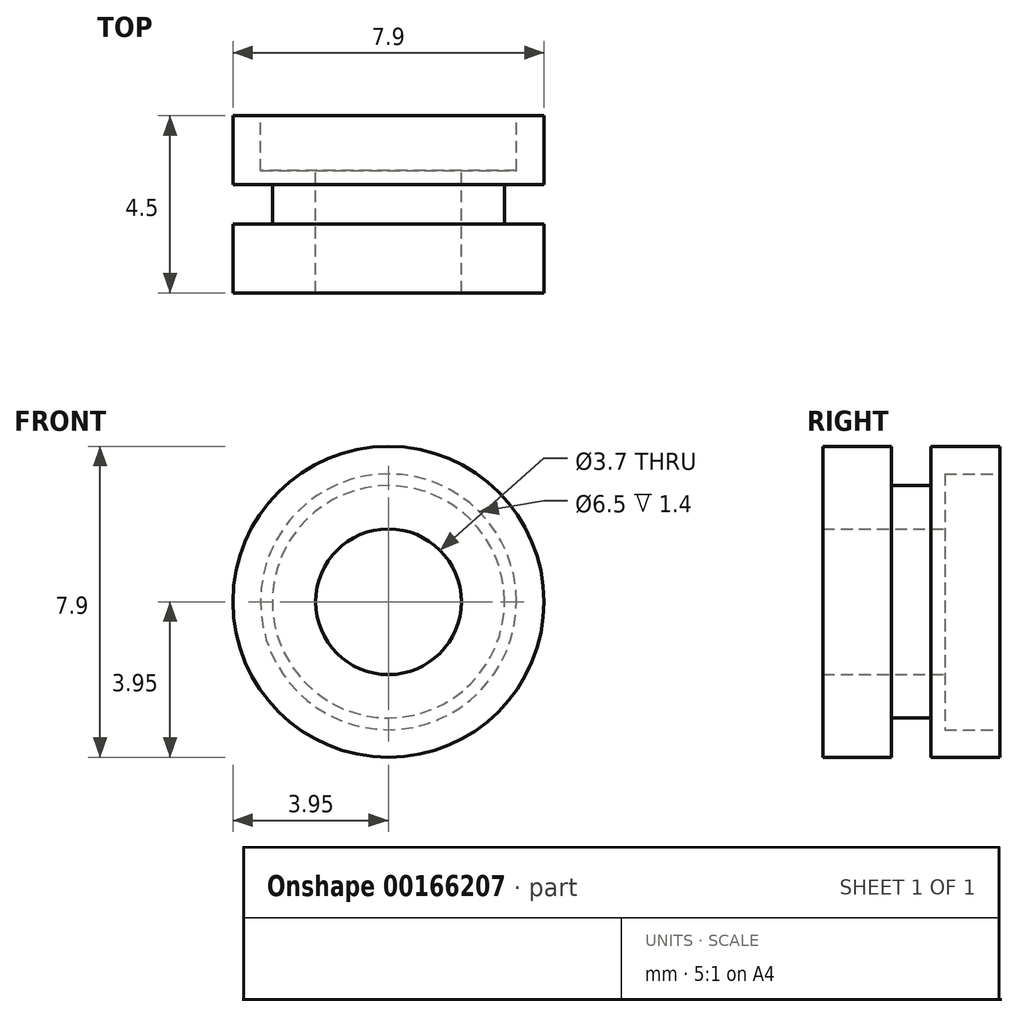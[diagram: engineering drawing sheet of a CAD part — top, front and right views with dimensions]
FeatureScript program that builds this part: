
annotation { "Feature Type Name" : "Feature", "Feature Type Description" : "" }
export const myFeature = defineFeature(function(context is Context, id is Id, definition is map)
    precondition{}
    {
        {
            var Q0;
            Q0=qCreatedBy(makeId("Right.planeOp"),FACE);
            var sketch = newSketch(context, id + "F0", { "sketchPlane" : qUnion([Q0])});
            skLineSegment(sketch, "E0", {"start": v(11.47, 0) * mm, "end": v(0, 0) * mm, "construction": true});
            skLineSegment(sketch, "E1", {"start": v(3.1, 1.85) * mm, "end": v(0, 1.85) * mm});
            skLineSegment(sketch, "E2", {"start": v(3.1, 1.85) * mm, "end": v(3.1, 3.25) * mm});
            skLineSegment(sketch, "E3", {"start": v(4.5, 3.25) * mm, "end": v(3.1, 3.25) * mm});
            skLineSegment(sketch, "E4", {"start": v(4.5, 3.25) * mm, "end": v(4.5, 3.95) * mm});
            skLineSegment(sketch, "E5", {"start": v(2.75, 3.95) * mm, "end": v(4.5, 3.95) * mm});
            skLineSegment(sketch, "E6", {"start": v(2.75, 3.95) * mm, "end": v(2.75, 2.95) * mm});
            skLineSegment(sketch, "E7", {"start": v(1.75, 2.95) * mm, "end": v(2.75, 2.95) * mm});
            skLineSegment(sketch, "E8", {"start": v(1.75, 2.95) * mm, "end": v(1.75, 3.95) * mm});
            skLineSegment(sketch, "E9", {"start": v(0, 3.95) * mm, "end": v(1.75, 3.95) * mm});
            skLineSegment(sketch, "E10", {"start": v(0, 3.95) * mm, "end": v(0, 1.85) * mm});
            skSolve(sketch);
        }
        {
            var Q0;
            Q0=makeQuery(id+"F0.imprint","IMPRINT",FACE,{"disambiguationData":[TD([[makeQuery(id+"F0.imprint","IMPRINT",EDGE,{"derivedFrom":sQuery(id+"F0.wireOp",EDGE,"E1")}),-1.0]])]});
            var Q1;
            Q1=sQuery(id+"F0.wireOp",EDGE,"E0");
            revolve(context, id + "F1", {"entities" : qUnion([Q0]), "axis" : qUnion([Q1]), "revolveType" : RevolveType.FULL});
        }
    });
